FCSTD DOCUMENT  (FreeCAD 0.19R14555 (Git shallow))
Label: 1U_Spacer_v0
License: All rights reserved
LicenseURL: http://en.wikipedia.org/wiki/All_rights_reserved
objects: Sketcher::SketchObject×1, PartDesign::Body×1
note: 2 computed .brp shape members not serialized (recipe doc carries the construction recipe); baked Part::Feature solids carry a one-line shape summary decoded from their .brp

FEATURE [Sketcher::SketchObject] Sketch
  FullyConstrained = true
  MapMode = 5
  Placement = pos=(0,0,0) rot=(1,0,0;1.5708rad)
  Support = -> [XZ_Plane]
  expr: Constraints[30] = 44.45 / 2
  expr: Constraints[28] = 31.75 / 2 + 2
  expr: Constraints[27] = 44.45 - 6.35 * 2
  sketch-geometry (11):
    g0: LineSegment StartX=0 StartY=0 StartZ=0 EndX=15.88 EndY=0 EndZ=0
    g1: LineSegment StartX=15.88 StartY=0 StartZ=0 EndX=15.88 EndY=44.45 EndZ=0
    g2: LineSegment StartX=15.88 StartY=44.45 StartZ=0 EndX=0 EndY=44.45 EndZ=0
    g3: LineSegment StartX=0 StartY=44.45 StartZ=0 EndX=0 EndY=0 EndZ=0
    g4: Circle CenterX=7.94 CenterY=6.35 CenterZ=0 NormalX=0 NormalY=0 NormalZ=1 AngleXU=0 Radius=2.775
    g5: Circle CenterX=7.94 CenterY=38.1 CenterZ=0 NormalX=0 NormalY=0 NormalZ=1 AngleXU=0 Radius=2.775
    g6: LineSegment StartX=15.88 StartY=44.45 StartZ=0 EndX=51.635 EndY=44.45 EndZ=0
    g7: LineSegment StartX=51.635 StartY=44.45 StartZ=0 EndX=51.635 EndY=0 EndZ=0
    g8: LineSegment StartX=51.635 StartY=0 StartZ=0 EndX=15.88 EndY=0 EndZ=0
    g9: LineSegment StartX=15.88 StartY=0 StartZ=0 EndX=15.88 EndY=44.45 EndZ=0
    g10: Circle CenterX=33.755 CenterY=22.225 CenterZ=0 NormalX=0 NormalY=0 NormalZ=1 AngleXU=0 Radius=15.875
  constraints (31):
    c: Coincident(g0,g1)
    c: Coincident(g1,g2)
    c: Coincident(g2,g3)
    c: Coincident(g3,g0)
    c: Horizontal(g0)
    c: Horizontal(g2)
    c: Vertical(g1)
    c: Vertical(g3)
    c: Coincident(g0,g-1)
    c: DistanceY(g3,g3) = 44.45
    c: Diameter(g4) = 5.55
    c: DistanceX(g0,g4) = 7.94
    c: DistanceY(g0,g4) = 6.35
    c: Equal(g4,g5) = 5.55
    c: Vertical(g5,g4)
    c: DistanceY(g5,g2) = 6.35
    c: DistanceX(g4,g0) = 7.94
    c: Coincident(g6,g7)
    c: Coincident(g7,g8)
    c: Coincident(g8,g9)
    c: Coincident(g9,g6)
    c: Horizontal(g6)
    c: Horizontal(g8)
    c: Vertical(g7)
    c: Vertical(g9)
    c: Coincident(g6,g1)
    c: PointOnObject(g7,g-1)
    c: Diameter(g10) = 31.75
    c: DistanceX(g1,g10) = 17.875
    c: DistanceX(g10,g7) = 17.88
    c: DistanceY(g7,g10) = 22.225
FEATURE [PartDesign::Body] Body
  Group = -> [Sketch]
  Origin = -> Origin
